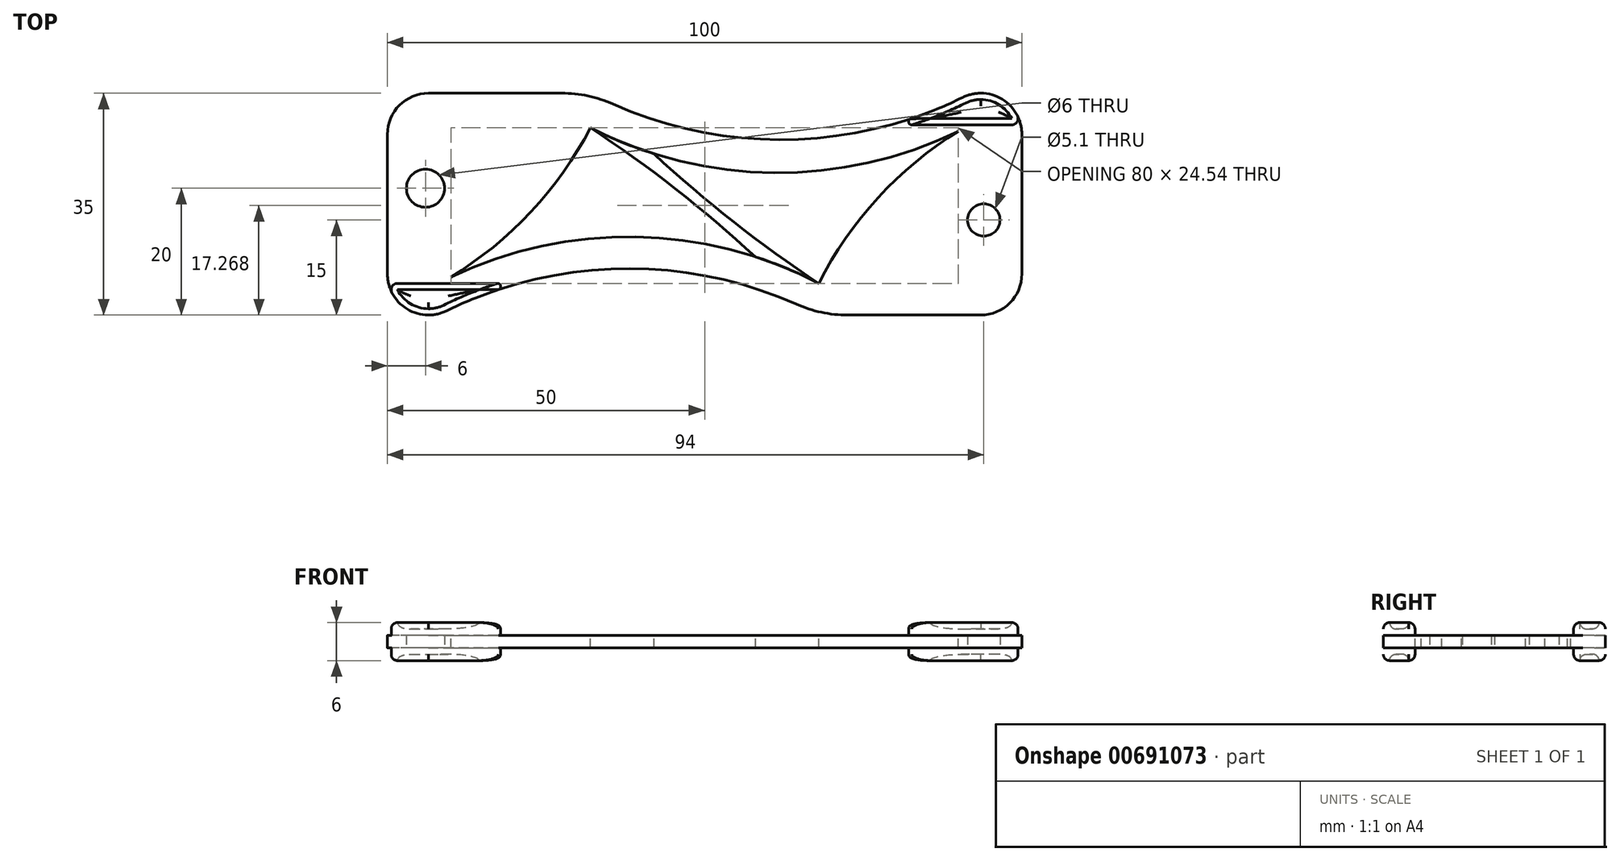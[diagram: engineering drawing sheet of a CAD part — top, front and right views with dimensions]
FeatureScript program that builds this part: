
annotation { "Feature Type Name" : "Feature", "Feature Type Description" : "" }
export const myFeature = defineFeature(function(context is Context, id is Id, definition is map)
    precondition{}
    {
        {
            var Q0;
            Q0=qCreatedBy(makeId("Top.planeOp"),FACE);
            var sketch = newSketch(context, id + "F0", { "sketchPlane" : qUnion([Q0])});
            skLineSegment(sketch, "E0.bottom", {"start": v(-68, -35) * mm, "end": v(-60, -35) * mm});
            skLineSegment(sketch, "E0.top", {"start": v(-68, 0) * mm, "end": v(-36, 0) * mm});
            skLineSegment(sketch, "E0.left", {"start": v(-68, -35) * mm, "end": v(-68, 0) * mm});
            skLineSegment(sketch, "E0.right", {"start": v(32, -35) * mm, "end": v(32, 0) * mm});
            skArc(sketch, "E1", {"start": v(0, -35) * mm, "mid": v(-30, -27.66) * mm, "end": v(-60, -35) * mm});
            skArc(sketch, "E2", {"start": v(-36, 0) * mm, "mid": v(-6, -7.34) * mm, "end": v(24, 0) * mm});
            skCircle(sketch, "E3", {"center": v(-62, -15) * mm, "radius": 3 * mm});
            skCircle(sketch, "E4", {"center": v(26, -20) * mm, "radius": 2.55 * mm});
            skLineSegment(sketch, "E5.trimOffspring", {"start": v(0, -35) * mm, "end": v(32, -35) * mm});
            skLineSegment(sketch, "E6.trimOffspring", {"start": v(24, 0) * mm, "end": v(32, 0) * mm});
            skSolve(sketch);
        }
        {
            var Q0;
            Q0 = qSketchRegion(id + "F0", true);
            extrude(context, id + "F1", {"entities" : qUnion([Q0]), "depth" : 2 * mm, "offsetDistance" : 25 * mm});
        }
        {
            var Q0;
            Q0=makeQuery(id+"F1.opExtrude","CAP_FACE",FACE,{"disambiguationData":[OSD([sQuery(id+"F0.wireOp",EDGE,"E0.bottom"),sQuery(id+"F0.wireOp",EDGE,"E0.top"),sQuery(id+"F0.wireOp",EDGE,"E0.left"),sQuery(id+"F0.wireOp",EDGE,"E0.right"),sQuery(id+"F0.wireOp",EDGE,"E1"),sQuery(id+"F0.wireOp",EDGE,"E2"),sQuery(id+"F0.wireOp",EDGE,"E3"),sQuery(id+"F0.wireOp",EDGE,"E4"),sQuery(id+"F0.wireOp",EDGE,"E5.trimOffspring"),sQuery(id+"F0.wireOp",EDGE,"E6.trimOffspring")])],"isStart":false});
            var sketch = newSketch(context, id + "F2", { "sketchPlane" : qUnion([Q0])});
            skLineSegment(sketch, "E7", {"start": v(-68, -30) * mm, "end": v(-54.55, -30) * mm});
            skLineSegment(sketch, "E8", {"start": v(32, -5) * mm, "end": v(20.4, -5) * mm});
            skLineSegment(sketch, "E9", {"start": v(20.4, -5) * mm, "end": v(11.27, -5) * mm});
            skLineSegment(sketch, "E10", {"start": v(-54.55, -30) * mm, "end": v(-47.27, -30) * mm});
            skLineSegment(sketch, "E11", {"start": v(-68, -30) * mm, "end": v(-68, -35) * mm});
            skLineSegment(sketch, "E12", {"start": v(-68, -35) * mm, "end": v(-60, -35) * mm});
            skLineSegment(sketch, "E13", {"start": v(32, -5) * mm, "end": v(32, 0) * mm});
            skLineSegment(sketch, "E14", {"start": v(32, 0) * mm, "end": v(24, 0) * mm});
            skArc(sketch, "E15", {"start": v(11.27, -5) * mm, "mid": v(17.77, -2.84) * mm, "end": v(24, 0) * mm});
            skArc(sketch, "E16", {"start": v(-47.27, -30) * mm, "mid": v(-53.77, -32.16) * mm, "end": v(-60, -35) * mm});
            skSolve(sketch);
        }
        {
            var Q0;
            Q0 = qSketchRegion(id + "F2", true);
            extrude(context, id + "F3", {"entities" : qUnion([Q0]), "operationType" : NewBodyOperationType.ADD, "depth" : 2 * mm, "offsetDistance" : 25 * mm, "hasSecondDirection" : true, "secondDirectionOppositeDirection" : true, "secondDirectionDepth" : 4 * mm});
        }
        {
            var Q0;
            Q0=makeQuery(id+"F3.boolean.opBoolean","MERGE",EDGE,{"derivedFrom":[makeQuery(id+"F1.opExtrude","SWEPT_EDGE",EDGE,{"disambiguationData":[OSD([sQuery(id+"F0.wireOp",EDGE,"E0.bottom"),sQuery(id+"F0.wireOp",EDGE,"E0.left")])]}),makeQuery(id+"F3.opExtrude","SWEPT_EDGE",EDGE,{"disambiguationData":[OSD([sQuery(id+"F2.wireOp",EDGE,"E11"),sQuery(id+"F2.wireOp",EDGE,"E12")])]})]});
            var Q1;
            Q1=makeQuery(id+"F3.boolean.opBoolean","MERGE",EDGE,{"derivedFrom":[makeQuery(id+"F1.opExtrude","SWEPT_EDGE",EDGE,{"disambiguationData":[OSD([sQuery(id+"F0.wireOp",EDGE,"E0.right"),sQuery(id+"F0.wireOp",EDGE,"E6.trimOffspring")])]}),makeQuery(id+"F3.opExtrude","SWEPT_EDGE",EDGE,{"disambiguationData":[OSD([sQuery(id+"F2.wireOp",EDGE,"E13"),sQuery(id+"F2.wireOp",EDGE,"E14")])]})]});
            var Q2;
            Q2=makeQuery(id+"F3.boolean.opBoolean","MERGE",EDGE,{"derivedFrom":[makeQuery(id+"F1.opExtrude","SWEPT_EDGE",EDGE,{"disambiguationData":[OSD([sQuery(id+"F0.wireOp",EDGE,"E2"),sQuery(id+"F0.wireOp",EDGE,"E6.trimOffspring")])]}),makeQuery(id+"F3.opExtrude","SWEPT_EDGE",EDGE,{"disambiguationData":[OSD([sQuery(id+"F2.wireOp",EDGE,"E14"),sQuery(id+"F2.wireOp",EDGE,"E15")])]})]});
            var Q3;
            Q3=makeQuery(id+"F3.boolean.opBoolean","MERGE",EDGE,{"derivedFrom":[makeQuery(id+"F1.opExtrude","SWEPT_EDGE",EDGE,{"disambiguationData":[OSD([sQuery(id+"F0.wireOp",EDGE,"E0.bottom"),sQuery(id+"F0.wireOp",EDGE,"E1")])]}),makeQuery(id+"F3.opExtrude","SWEPT_EDGE",EDGE,{"disambiguationData":[OSD([sQuery(id+"F2.wireOp",EDGE,"E12"),sQuery(id+"F2.wireOp",EDGE,"E16")])]})]});
            var Q4;
            Q4=makeQuery(id+"F1.opExtrude","SWEPT_EDGE",EDGE,{"disambiguationData":[OSD([sQuery(id+"F0.wireOp",EDGE,"E0.top"),sQuery(id+"F0.wireOp",EDGE,"E0.left")])]});
            var Q5;
            Q5=makeQuery(id+"F1.opExtrude","SWEPT_EDGE",EDGE,{"disambiguationData":[OSD([sQuery(id+"F0.wireOp",EDGE,"E0.right"),sQuery(id+"F0.wireOp",EDGE,"E5.trimOffspring")])]});
            fillet(context, id + "F4", {"entities" : qUnion([Q0, Q1, Q2, Q3, Q4, Q5]), "radius" : 6.5 * mm, "tangentPropagation" : true, "allowEdgeOverflow" : false});
        }
        {
            var Q0;
            Q0=makeQuery(id+"F1.opExtrude","SWEPT_EDGE",EDGE,{"disambiguationData":[OSD([sQuery(id+"F0.wireOp",EDGE,"E1"),sQuery(id+"F0.wireOp",EDGE,"E5.trimOffspring")])]});
            var Q1;
            Q1=makeQuery(id+"F1.opExtrude","SWEPT_EDGE",EDGE,{"disambiguationData":[OSD([sQuery(id+"F0.wireOp",EDGE,"E0.top"),sQuery(id+"F0.wireOp",EDGE,"E2")])]});
            fillet(context, id + "F5", {"entities" : qUnion([Q0, Q1]), "radius" : 20 * mm, "tangentPropagation" : true, "allowEdgeOverflow" : false});
        }
        {
            var Q0;
            {var subQ0=sQuery(id+"F2.wireOp",EDGE,"E16");var subQ1=sQuery(id+"F2.wireOp",EDGE,"E12");var subQ2=sQuery(id+"F2.wireOp",EDGE,"E11");var subQ3=sQuery(id+"F2.wireOp",EDGE,"E10");var subQ4=sQuery(id+"F2.wireOp",EDGE,"E7");var subQ6=sQuery(id+"F0.wireOp",EDGE,"E0.left");var subQ7=sQuery(id+"F0.wireOp",EDGE,"E0.bottom");Q0=makeQuery(id+"F4.opFillet","BLEND_EDGE",EDGE,{"blendedFrom":[makeQuery(id+"F3.boolean.opBoolean","MERGE",EDGE,{"derivedFrom":[makeQuery(id+"F1.opExtrude","SWEPT_EDGE",EDGE,{"disambiguationData":[OSD([subQ7,subQ6])]}),makeQuery(id+"F3.opExtrude","SWEPT_EDGE",EDGE,{"disambiguationData":[OSD([subQ2,subQ1])]})]}),makeQuery(id+"F3.boolean.opBoolean","SPLIT",FACE,{"disambiguationData":[TD([makeQuery(id+"F3.opExtrude","CAP_FACE",FACE,{"disambiguationData":[OSD([subQ4,subQ3,subQ2,subQ1,subQ0])],"isStart":false})])],"derivedFrom":makeQuery(id+"F3.opExtrude","SWEPT_FACE",FACE,{"disambiguationData":[OSD([subQ4,subQ3])]})})],"blendedInto":[makeQuery(id+"F3.boolean.opBoolean","SPLIT",FACE,{"disambiguationData":[TD([makeQuery(id+"F3.opExtrude","CAP_FACE",FACE,{"disambiguationData":[OSD([subQ4,subQ3,subQ2,subQ1,subQ0])],"isStart":false})])],"derivedFrom":makeQuery(id+"F3.opExtrude","SWEPT_FACE",FACE,{"disambiguationData":[OSD([subQ4,subQ3])]})})]});}
            var Q1;
            {var subQ0=sQuery(id+"F2.wireOp",EDGE,"E16");var subQ1=sQuery(id+"F2.wireOp",EDGE,"E12");var subQ2=sQuery(id+"F2.wireOp",EDGE,"E11");var subQ3=sQuery(id+"F2.wireOp",EDGE,"E10");var subQ4=sQuery(id+"F2.wireOp",EDGE,"E7");var subQ5=sQuery(id+"F0.wireOp",EDGE,"E0.left");var subQ7=sQuery(id+"F0.wireOp",EDGE,"E0.bottom");Q1=makeQuery(id+"F4.opFillet","BLEND_EDGE",EDGE,{"blendedFrom":[makeQuery(id+"F3.boolean.opBoolean","MERGE",EDGE,{"derivedFrom":[makeQuery(id+"F1.opExtrude","SWEPT_EDGE",EDGE,{"disambiguationData":[OSD([subQ7,subQ5])]}),makeQuery(id+"F3.opExtrude","SWEPT_EDGE",EDGE,{"disambiguationData":[OSD([subQ2,subQ1])]})]}),makeQuery(id+"F3.boolean.opBoolean","SPLIT",FACE,{"disambiguationData":[TD([makeQuery(id+"F3.opExtrude","CAP_FACE",FACE,{"disambiguationData":[OSD([subQ4,subQ3,subQ2,subQ1,subQ0])],"isStart":true})])],"derivedFrom":makeQuery(id+"F3.opExtrude","SWEPT_FACE",FACE,{"disambiguationData":[OSD([subQ4,subQ3])]})})],"blendedInto":[makeQuery(id+"F3.boolean.opBoolean","SPLIT",FACE,{"disambiguationData":[TD([makeQuery(id+"F3.opExtrude","CAP_FACE",FACE,{"disambiguationData":[OSD([subQ4,subQ3,subQ2,subQ1,subQ0])],"isStart":true})])],"derivedFrom":makeQuery(id+"F3.opExtrude","SWEPT_FACE",FACE,{"disambiguationData":[OSD([subQ4,subQ3])]})})]});}
            var Q2;
            {var subQ0=sQuery(id+"F2.wireOp",EDGE,"E15");var subQ1=sQuery(id+"F2.wireOp",EDGE,"E14");var subQ2=sQuery(id+"F2.wireOp",EDGE,"E13");var subQ3=sQuery(id+"F2.wireOp",EDGE,"E9");var subQ4=sQuery(id+"F2.wireOp",EDGE,"E8");var subQ5=sQuery(id+"F0.wireOp",EDGE,"E0.right");var subQ7=sQuery(id+"F0.wireOp",EDGE,"E6.trimOffspring");Q2=makeQuery(id+"F4.opFillet","BLEND_EDGE",EDGE,{"blendedFrom":[makeQuery(id+"F3.boolean.opBoolean","MERGE",EDGE,{"derivedFrom":[makeQuery(id+"F1.opExtrude","SWEPT_EDGE",EDGE,{"disambiguationData":[OSD([subQ5,subQ7])]}),makeQuery(id+"F3.opExtrude","SWEPT_EDGE",EDGE,{"disambiguationData":[OSD([subQ2,subQ1])]})]}),makeQuery(id+"F3.boolean.opBoolean","SPLIT",FACE,{"disambiguationData":[TD([makeQuery(id+"F3.opExtrude","CAP_FACE",FACE,{"disambiguationData":[OSD([subQ4,subQ3,subQ2,subQ1,subQ0])],"isStart":false})])],"derivedFrom":makeQuery(id+"F3.opExtrude","SWEPT_FACE",FACE,{"disambiguationData":[OSD([subQ4,subQ3])]})})],"blendedInto":[makeQuery(id+"F3.boolean.opBoolean","SPLIT",FACE,{"disambiguationData":[TD([makeQuery(id+"F3.opExtrude","CAP_FACE",FACE,{"disambiguationData":[OSD([subQ4,subQ3,subQ2,subQ1,subQ0])],"isStart":false})])],"derivedFrom":makeQuery(id+"F3.opExtrude","SWEPT_FACE",FACE,{"disambiguationData":[OSD([subQ4,subQ3])]})})]});}
            var Q3;
            {var subQ0=sQuery(id+"F2.wireOp",EDGE,"E15");var subQ1=sQuery(id+"F2.wireOp",EDGE,"E14");var subQ2=sQuery(id+"F2.wireOp",EDGE,"E13");var subQ3=sQuery(id+"F2.wireOp",EDGE,"E9");var subQ4=sQuery(id+"F2.wireOp",EDGE,"E8");var subQ5=sQuery(id+"F0.wireOp",EDGE,"E0.right");var subQ7=sQuery(id+"F0.wireOp",EDGE,"E6.trimOffspring");Q3=makeQuery(id+"F4.opFillet","BLEND_EDGE",EDGE,{"blendedFrom":[makeQuery(id+"F3.boolean.opBoolean","MERGE",EDGE,{"derivedFrom":[makeQuery(id+"F1.opExtrude","SWEPT_EDGE",EDGE,{"disambiguationData":[OSD([subQ5,subQ7])]}),makeQuery(id+"F3.opExtrude","SWEPT_EDGE",EDGE,{"disambiguationData":[OSD([subQ2,subQ1])]})]}),makeQuery(id+"F3.boolean.opBoolean","SPLIT",FACE,{"disambiguationData":[TD([makeQuery(id+"F3.opExtrude","CAP_FACE",FACE,{"disambiguationData":[OSD([subQ4,subQ3,subQ2,subQ1,subQ0])],"isStart":true})])],"derivedFrom":makeQuery(id+"F3.opExtrude","SWEPT_FACE",FACE,{"disambiguationData":[OSD([subQ4,subQ3])]})})],"blendedInto":[makeQuery(id+"F3.boolean.opBoolean","SPLIT",FACE,{"disambiguationData":[TD([makeQuery(id+"F3.opExtrude","CAP_FACE",FACE,{"disambiguationData":[OSD([subQ4,subQ3,subQ2,subQ1,subQ0])],"isStart":true})])],"derivedFrom":makeQuery(id+"F3.opExtrude","SWEPT_FACE",FACE,{"disambiguationData":[OSD([subQ4,subQ3])]})})]});}
            fillet(context, id + "F6", {"entities" : qUnion([Q0, Q1, Q2, Q3]), "radius" : 1 * mm, "tangentPropagation" : true, "allowEdgeOverflow" : false});
        }
        {
            var Q0;
            {var subQ0=sQuery(id+"F2.wireOp",EDGE,"E15");var subQ1=sQuery(id+"F2.wireOp",EDGE,"E9");var subQ2=sQuery(id+"F2.wireOp",EDGE,"E8");var subQ3=sQuery(id+"F0.wireOp",EDGE,"E2");Q0=makeQuery(id+"F3.boolean.opBoolean","SPLIT",EDGE,{"disambiguationData":[TD([makeQuery(id+"F3.opExtrude","CAP_FACE",FACE,{"disambiguationData":[OSD([subQ2,subQ1,sQuery(id+"F2.wireOp",EDGE,"E13"),sQuery(id+"F2.wireOp",EDGE,"E14"),subQ0])],"isStart":false})])],"derivedFrom":makeQuery(id+"F3.opExtrude","SWEPT_EDGE",EDGE,{"disambiguationData":[OSD([subQ3,subQ1,subQ0])]})});}
            var Q1;
            {var subQ0=sQuery(id+"F2.wireOp",EDGE,"E15");var subQ1=sQuery(id+"F2.wireOp",EDGE,"E9");var subQ2=sQuery(id+"F2.wireOp",EDGE,"E8");var subQ3=sQuery(id+"F0.wireOp",EDGE,"E2");Q1=makeQuery(id+"F3.boolean.opBoolean","SPLIT",EDGE,{"disambiguationData":[TD([makeQuery(id+"F3.opExtrude","CAP_FACE",FACE,{"disambiguationData":[OSD([subQ2,subQ1,sQuery(id+"F2.wireOp",EDGE,"E13"),sQuery(id+"F2.wireOp",EDGE,"E14"),subQ0])],"isStart":true})])],"derivedFrom":makeQuery(id+"F3.opExtrude","SWEPT_EDGE",EDGE,{"disambiguationData":[OSD([subQ3,subQ1,subQ0])]})});}
            var Q2;
            {var subQ0=sQuery(id+"F2.wireOp",EDGE,"E16");var subQ1=sQuery(id+"F2.wireOp",EDGE,"E10");var subQ2=sQuery(id+"F2.wireOp",EDGE,"E7");var subQ3=sQuery(id+"F0.wireOp",EDGE,"E1");Q2=makeQuery(id+"F3.boolean.opBoolean","SPLIT",EDGE,{"disambiguationData":[TD([makeQuery(id+"F3.opExtrude","CAP_FACE",FACE,{"disambiguationData":[OSD([subQ2,subQ1,sQuery(id+"F2.wireOp",EDGE,"E11"),sQuery(id+"F2.wireOp",EDGE,"E12"),subQ0])],"isStart":false})])],"derivedFrom":makeQuery(id+"F3.opExtrude","SWEPT_EDGE",EDGE,{"disambiguationData":[OSD([subQ3,subQ1,subQ0])]})});}
            var Q3;
            {var subQ0=sQuery(id+"F2.wireOp",EDGE,"E16");var subQ1=sQuery(id+"F2.wireOp",EDGE,"E10");var subQ2=sQuery(id+"F2.wireOp",EDGE,"E7");var subQ3=sQuery(id+"F0.wireOp",EDGE,"E1");Q3=makeQuery(id+"F3.boolean.opBoolean","SPLIT",EDGE,{"disambiguationData":[TD([makeQuery(id+"F3.opExtrude","CAP_FACE",FACE,{"disambiguationData":[OSD([subQ2,subQ1,sQuery(id+"F2.wireOp",EDGE,"E11"),sQuery(id+"F2.wireOp",EDGE,"E12"),subQ0])],"isStart":true})])],"derivedFrom":makeQuery(id+"F3.opExtrude","SWEPT_EDGE",EDGE,{"disambiguationData":[OSD([subQ3,subQ1,subQ0])]})});}
            fillet(context, id + "F7", {"entities" : qUnion([Q0, Q1, Q2, Q3]), "radius" : 0.5 * mm, "tangentPropagation" : true, "allowEdgeOverflow" : false});
        }
        {
            var Q0;
            Q0=makeQuery(id+"F3.opExtrude","CAP_EDGE",EDGE,{"disambiguationData":[OSD([sQuery(id+"F2.wireOp",EDGE,"E8"),sQuery(id+"F2.wireOp",EDGE,"E9")])],"isStart":false});
            var Q1;
            Q1=makeQuery(id+"F3.opExtrude","CAP_FACE",FACE,{"disambiguationData":[OSD([sQuery(id+"F2.wireOp",EDGE,"E8"),sQuery(id+"F2.wireOp",EDGE,"E9"),sQuery(id+"F2.wireOp",EDGE,"E13"),sQuery(id+"F2.wireOp",EDGE,"E14"),sQuery(id+"F2.wireOp",EDGE,"E15")])],"isStart":false});
            var Q2;
            Q2=makeQuery(id+"F3.opExtrude","CAP_FACE",FACE,{"disambiguationData":[OSD([sQuery(id+"F2.wireOp",EDGE,"E8"),sQuery(id+"F2.wireOp",EDGE,"E9"),sQuery(id+"F2.wireOp",EDGE,"E13"),sQuery(id+"F2.wireOp",EDGE,"E14"),sQuery(id+"F2.wireOp",EDGE,"E15")])],"isStart":true});
            var Q3;
            Q3=makeQuery(id+"F3.opExtrude","CAP_FACE",FACE,{"disambiguationData":[OSD([sQuery(id+"F2.wireOp",EDGE,"E7"),sQuery(id+"F2.wireOp",EDGE,"E10"),sQuery(id+"F2.wireOp",EDGE,"E11"),sQuery(id+"F2.wireOp",EDGE,"E12"),sQuery(id+"F2.wireOp",EDGE,"E16")])],"isStart":false});
            var Q4;
            Q4=makeQuery(id+"F3.opExtrude","CAP_FACE",FACE,{"disambiguationData":[OSD([sQuery(id+"F2.wireOp",EDGE,"E7"),sQuery(id+"F2.wireOp",EDGE,"E10"),sQuery(id+"F2.wireOp",EDGE,"E11"),sQuery(id+"F2.wireOp",EDGE,"E12"),sQuery(id+"F2.wireOp",EDGE,"E16")])],"isStart":true});
            fillet(context, id + "F8", {"entities" : qUnion([Q0, Q1, Q2, Q3, Q4]), "radius" : 1 * mm, "tangentPropagation" : true, "allowEdgeOverflow" : false});
        }
        {
            var Q0;
            Q0=makeQuery(id+"F3.opExtrude","CAP_FACE",FACE,{"disambiguationData":[OSD([sQuery(id+"F2.wireOp",EDGE,"E7"),sQuery(id+"F2.wireOp",EDGE,"E10"),sQuery(id+"F2.wireOp",EDGE,"E11"),sQuery(id+"F2.wireOp",EDGE,"E12"),sQuery(id+"F2.wireOp",EDGE,"E16")])],"isStart":false});
            var Q1;
            Q1=makeQuery(id+"F3.opExtrude","CAP_FACE",FACE,{"disambiguationData":[OSD([sQuery(id+"F2.wireOp",EDGE,"E8"),sQuery(id+"F2.wireOp",EDGE,"E9"),sQuery(id+"F2.wireOp",EDGE,"E13"),sQuery(id+"F2.wireOp",EDGE,"E14"),sQuery(id+"F2.wireOp",EDGE,"E15")])],"isStart":false});
            extrude(context, id + "F9", {"entities" : qUnion([Q0, Q1]), "operationType" : NewBodyOperationType.REMOVE, "oppositeDirection" : true, "depth" : 1 * mm, "offsetDistance" : 25 * mm});
        }
        {
            var Q0;
            Q0=makeQuery(id+"F3.opExtrude","CAP_FACE",FACE,{"disambiguationData":[OSD([sQuery(id+"F2.wireOp",EDGE,"E7"),sQuery(id+"F2.wireOp",EDGE,"E10"),sQuery(id+"F2.wireOp",EDGE,"E11"),sQuery(id+"F2.wireOp",EDGE,"E12"),sQuery(id+"F2.wireOp",EDGE,"E16")])],"isStart":true});
            var Q1;
            Q1=makeQuery(id+"F3.opExtrude","CAP_FACE",FACE,{"disambiguationData":[OSD([sQuery(id+"F2.wireOp",EDGE,"E8"),sQuery(id+"F2.wireOp",EDGE,"E9"),sQuery(id+"F2.wireOp",EDGE,"E13"),sQuery(id+"F2.wireOp",EDGE,"E14"),sQuery(id+"F2.wireOp",EDGE,"E15")])],"isStart":true});
            extrude(context, id + "F10", {"entities" : qUnion([Q0, Q1]), "operationType" : NewBodyOperationType.REMOVE, "oppositeDirection" : true, "depth" : 1 * mm, "offsetDistance" : 25 * mm});
        }
        {
            var Q0;
            Q0=makeQuery(id+"F10.boolean.opBoolean","COPY",FACE,{"derivedFrom":makeQuery(id+"F10.opExtrude","CAP_FACE",FACE,{"disambiguationData":[OSD([sQuery(id+"F2.wireOp",EDGE,"E8"),sQuery(id+"F2.wireOp",EDGE,"E9"),sQuery(id+"F2.wireOp",EDGE,"E13"),sQuery(id+"F2.wireOp",EDGE,"E14"),sQuery(id+"F2.wireOp",EDGE,"E15")])],"isStart":false})});
            var Q1;
            Q1=makeQuery(id+"F9.boolean.opBoolean","COPY",FACE,{"derivedFrom":makeQuery(id+"F9.opExtrude","CAP_FACE",FACE,{"disambiguationData":[OSD([sQuery(id+"F2.wireOp",EDGE,"E8"),sQuery(id+"F2.wireOp",EDGE,"E9"),sQuery(id+"F2.wireOp",EDGE,"E13"),sQuery(id+"F2.wireOp",EDGE,"E14"),sQuery(id+"F2.wireOp",EDGE,"E15")])],"isStart":false})});
            var Q2;
            Q2=makeQuery(id+"F9.boolean.opBoolean","COPY",FACE,{"derivedFrom":makeQuery(id+"F9.opExtrude","CAP_FACE",FACE,{"disambiguationData":[OSD([sQuery(id+"F2.wireOp",EDGE,"E7"),sQuery(id+"F2.wireOp",EDGE,"E10"),sQuery(id+"F2.wireOp",EDGE,"E11"),sQuery(id+"F2.wireOp",EDGE,"E12"),sQuery(id+"F2.wireOp",EDGE,"E16")])],"isStart":false})});
            var Q3;
            Q3=makeQuery(id+"F10.boolean.opBoolean","COPY",FACE,{"derivedFrom":makeQuery(id+"F10.opExtrude","CAP_FACE",FACE,{"disambiguationData":[OSD([sQuery(id+"F2.wireOp",EDGE,"E7"),sQuery(id+"F2.wireOp",EDGE,"E10"),sQuery(id+"F2.wireOp",EDGE,"E11"),sQuery(id+"F2.wireOp",EDGE,"E12"),sQuery(id+"F2.wireOp",EDGE,"E16")])],"isStart":false})});
            fillet(context, id + "F11", {"entities" : qUnion([Q0, Q1, Q2, Q3]), "radius" : 1 * mm, "tangentPropagation" : true, "allowEdgeOverflow" : false});
        }
        {
            var Q0;
            Q0=makeQuery(id+"F1.opExtrude","CAP_FACE",FACE,{"disambiguationData":[OSD([sQuery(id+"F0.wireOp",EDGE,"E0.bottom"),sQuery(id+"F0.wireOp",EDGE,"E0.top"),sQuery(id+"F0.wireOp",EDGE,"E0.left"),sQuery(id+"F0.wireOp",EDGE,"E0.right"),sQuery(id+"F0.wireOp",EDGE,"E1"),sQuery(id+"F0.wireOp",EDGE,"E2"),sQuery(id+"F0.wireOp",EDGE,"E3"),sQuery(id+"F0.wireOp",EDGE,"E4"),sQuery(id+"F0.wireOp",EDGE,"E5.trimOffspring"),sQuery(id+"F0.wireOp",EDGE,"E6.trimOffspring")])],"isStart":false});
            var sketch = newSketch(context, id + "F12", { "sketchPlane" : qUnion([Q0])});
            skArc(sketch, "E17", {"start": v(22, -6) * mm, "mid": v(9.34, -16.48) * mm, "end": v(0, -30) * mm});
            skArc(sketch, "E18", {"start": v(-36, -5.46) * mm, "mid": v(-7.06, -12.56) * mm, "end": v(22, -6) * mm});
            skArc(sketch, "E19", {"start": v(-58, -29) * mm, "mid": v(-45.4, -18.74) * mm, "end": v(-36, -5.46) * mm});
            skArc(sketch, "E20", {"start": v(0, -30) * mm, "mid": v(-28.88, -22.67) * mm, "end": v(-58, -29) * mm});
            skSolve(sketch);
        }
        {
            var Q0;
            Q0 = qSketchRegion(id + "F12", true);
            extrude(context, id + "F13", {"entities" : qUnion([Q0]), "operationType" : NewBodyOperationType.REMOVE, "oppositeDirection" : true, "depth" : 25 * mm, "offsetDistance" : 25 * mm});
        }
        {
            var Q0;
            Q0=makeQuery(id+"F1.opExtrude","CAP_FACE",FACE,{"disambiguationData":[OSD([sQuery(id+"F0.wireOp",EDGE,"E0.bottom"),sQuery(id+"F0.wireOp",EDGE,"E0.top"),sQuery(id+"F0.wireOp",EDGE,"E0.left"),sQuery(id+"F0.wireOp",EDGE,"E0.right"),sQuery(id+"F0.wireOp",EDGE,"E1"),sQuery(id+"F0.wireOp",EDGE,"E2"),sQuery(id+"F0.wireOp",EDGE,"E3"),sQuery(id+"F0.wireOp",EDGE,"E4"),sQuery(id+"F0.wireOp",EDGE,"E5.trimOffspring"),sQuery(id+"F0.wireOp",EDGE,"E6.trimOffspring")])],"isStart":false});
            var sketch = newSketch(context, id + "F14", { "sketchPlane" : qUnion([Q0])});
            skArc(sketch, "E21", {"start": v(-10, -25.82) * mm, "mid": v(-22.58, -15.1) * mm, "end": v(-36, -5.46) * mm});
            skArc(sketch, "E22", {"start": v(-26, -9.56) * mm, "mid": v(-13.42, -20.32) * mm, "end": v(0, -30) * mm});
            skSolve(sketch);
        }
        {
            var Q0;
            Q0 = qSketchRegion(id + "F14", true);
            var Q1;
            {var subQ0=sQuery(id+"F14.wireOp",EDGE,"E21");Q1=makeQuery(id+"F14.imprint","IMPRINT",FACE,{"disambiguationData":[TD([[makeQuery(id+"F14.imprint","IMPRINT",EDGE,{"derivedFrom":subQ0}),-1.0]])]});}
            extrude(context, id + "F15", {"entities" : qUnion([Q0, Q1]), "oppositeDirection" : true, "depth" : 2 * mm, "offsetDistance" : 25 * mm});
        }
    });
